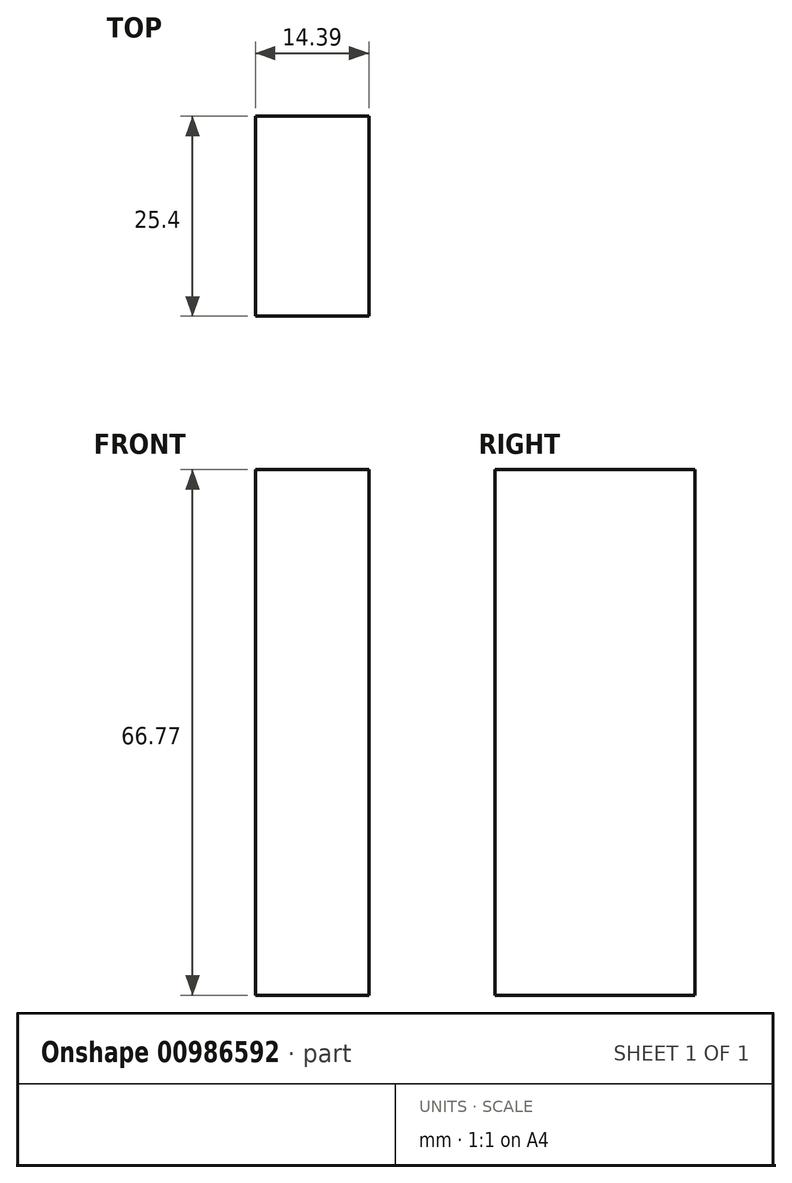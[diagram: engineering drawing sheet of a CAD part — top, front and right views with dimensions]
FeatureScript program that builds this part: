
annotation { "Feature Type Name" : "Feature", "Feature Type Description" : "" }
export const myFeature = defineFeature(function(context is Context, id is Id, definition is map)
    precondition{}
    {
        {
            var Q0;
            Q0=qCreatedBy(makeId("Front.planeOp"),FACE);
            var sketch = newSketch(context, id + "F0", { "sketchPlane" : qUnion([Q0])});
            skLineSegment(sketch, "E0.bottom", {"start": v(-4.17, -62.02) * mm, "end": v(10.22, -62.02) * mm});
            skLineSegment(sketch, "E0.top", {"start": v(-4.17, 4.75) * mm, "end": v(10.22, 4.75) * mm});
            skLineSegment(sketch, "E0.left", {"start": v(-4.17, -62.02) * mm, "end": v(-4.17, 4.75) * mm});
            skLineSegment(sketch, "E0.right", {"start": v(10.22, -62.02) * mm, "end": v(10.22, 4.75) * mm});
            skSolve(sketch);
        }
        {
            var Q0;
            Q0 = qSketchRegion(id + "F0", true);
            extrude(context, id + "F1", {"entities" : qUnion([Q0]), "depth" : 25.4 * mm, "offsetDistance" : 25.4 * mm});
        }
        {
            var Q0;
            Q0=qCreatedBy(makeId("Front.planeOp"),FACE);
            var sketch = newSketch(context, id + "F2", { "sketchPlane" : qUnion([Q0])});
            skCircle(sketch, "E1", {"center": v(2.45, 31.54) * mm, "radius": 16.72 * mm});
            skLineSegment(sketch, "E2", {"start": v(17.5, 24.28) * mm, "end": v(30.94, 12.82) * mm});
            skArc(sketch, "E3", {"start": v(30.94, 12.82) * mm, "mid": v(38.68, 16.53) * mm, "end": v(37.56, 25.03) * mm});
            skLineSegment(sketch, "E4", {"start": v(37.56, 25.03) * mm, "end": v(18.98, 29) * mm});
            skLineSegment(sketch, "E5.1.0", {"start": v(-29.78, 3.02) * mm, "end": v(-26.57, 20.38) * mm});
            skArc(sketch, "E5.1.1", {"start": v(-26.57, 20.38) * mm, "mid": v(-33.65, 25.23) * mm, "end": v(-40.46, 20.01) * mm});
            skLineSegment(sketch, "E5.1.2", {"start": v(-40.46, 20.01) * mm, "end": v(-34.61, 1.93) * mm});
            skLineSegment(sketch, "E5.2.0", {"start": v(12.27, -27.3) * mm, "end": v(-4.37, -33.2) * mm});
            skArc(sketch, "E5.2.1", {"start": v(-4.37, -33.2) * mm, "mid": v(-5.03, -41.76) * mm, "end": v(2.9, -45.04) * mm});
            skLineSegment(sketch, "E5.2.2", {"start": v(2.9, -45.04) * mm, "end": v(15.64, -30.94) * mm});
            skPoint(sketch, "E5.center", {"position": v(0, 0) * mm});
            skSolve(sketch);
        }
    });
